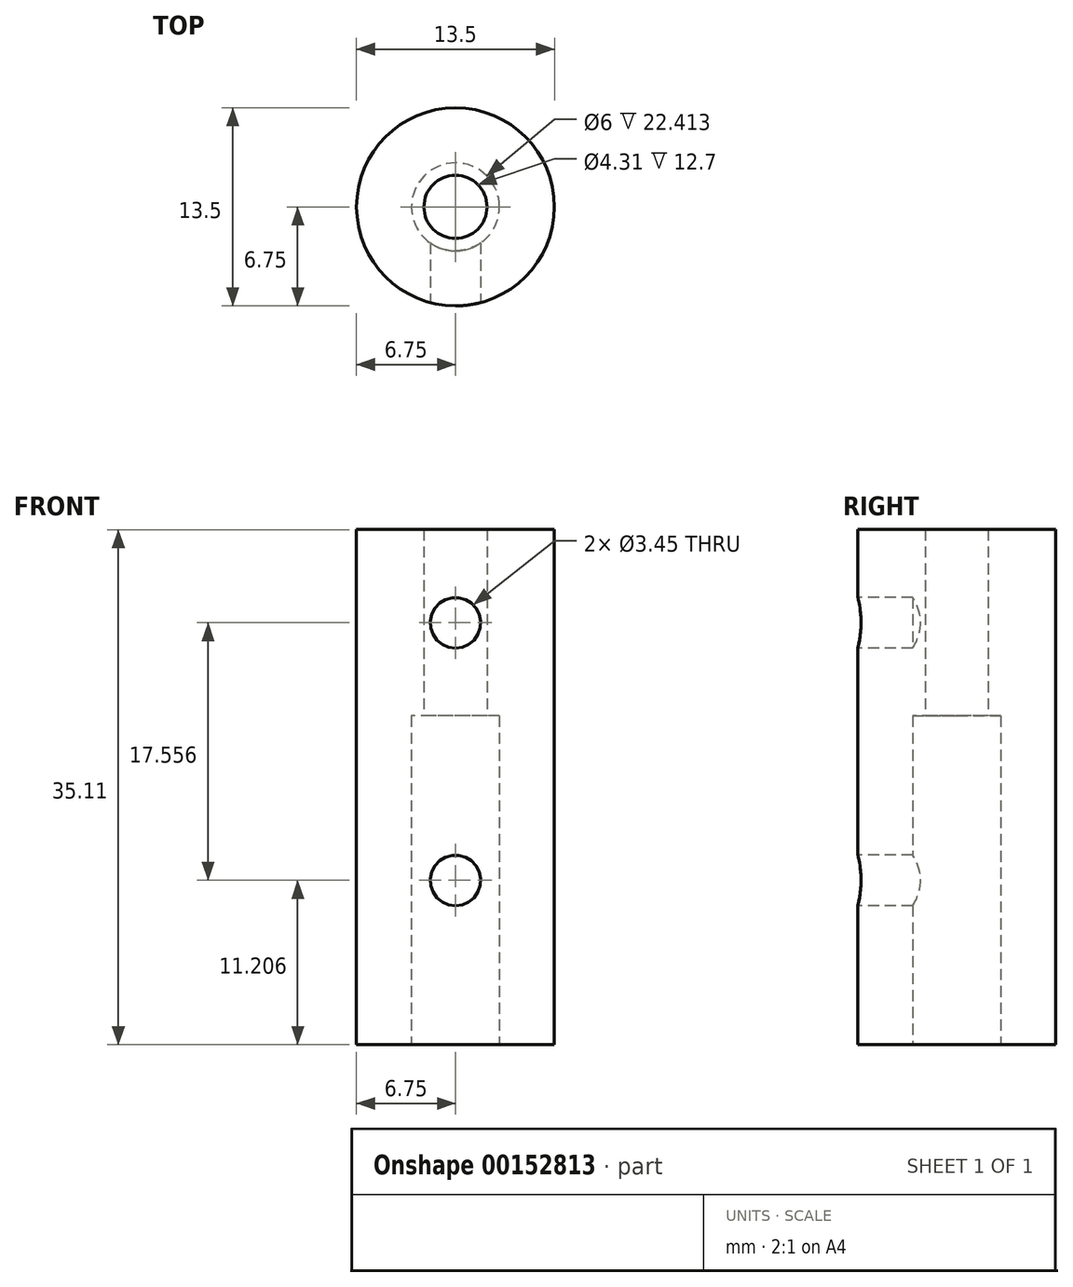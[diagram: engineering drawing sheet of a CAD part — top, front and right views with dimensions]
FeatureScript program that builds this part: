
annotation { "Feature Type Name" : "Feature", "Feature Type Description" : "" }
export const myFeature = defineFeature(function(context is Context, id is Id, definition is map)
    precondition{}
    {
        {
            var Q0;
            Q0=qCreatedBy(makeId("Top.planeOp"),FACE);
            var sketch = newSketch(context, id + "F0", { "sketchPlane" : qUnion([Q0])});
            skLineSegment(sketch, "E0.bottom", {"start": v(12.7, -12.7) * mm, "end": v(-12.7, -12.7) * mm});
            skLineSegment(sketch, "E0.top", {"start": v(12.7, 12.7) * mm, "end": v(-12.7, 12.7) * mm});
            skLineSegment(sketch, "E0.left", {"start": v(12.7, -12.7) * mm, "end": v(12.7, 12.7) * mm});
            skLineSegment(sketch, "E0.right", {"start": v(-12.7, -12.7) * mm, "end": v(-12.7, 12.7) * mm});
            skPoint(sketch, "E0.middle", {"position": v(0, 0) * mm});
            skCircle(sketch, "E1", {"center": v(0, 0) * mm, "radius": 12.7 * mm, "construction": true});
            skCircle(sketch, "E2", {"center": v(0, 0) * mm, "radius": 3 * mm});
            skCircle(sketch, "E3", {"center": v(0, 0) * mm, "radius": 3.18 * mm, "construction": true});
            skSolve(sketch);
        }
        {
            var Q0;
            Q0 = qSketchRegion(id + "F0", true);
            extrude(context, id + "F1", {"entities" : qUnion([Q0]), "depth" : 22.41 * mm});
        }
        {
            var Q0;
            Q0=makeQuery(id+"F1.opExtrude","CAP_FACE",FACE,{"disambiguationData":[OSD([sQuery(id+"F0.wireOp",EDGE,"E0.bottom"),sQuery(id+"F0.wireOp",EDGE,"E0.top"),sQuery(id+"F0.wireOp",EDGE,"E0.left"),sQuery(id+"F0.wireOp",EDGE,"E0.right"),sQuery(id+"F0.wireOp",EDGE,"E2")])],"isStart":false});
            var sketch = newSketch(context, id + "F2", { "sketchPlane" : qUnion([Q0])});
            skCircle(sketch, "E4", {"center": v(0, 0) * mm, "radius": 2.15 * mm});
            skSolve(sketch);
        }
        {
            var Q0;
            Q0=makeQuery(id+"F2.imprint","IMPRINT",FACE,{"disambiguationData":[TD([[makeQuery(id+"F2.imprint","IMPRINT",EDGE,{"derivedFrom":sQuery(id+"F2.wireOp",EDGE,"E4")}),-1.0]])]});
            var Q1;
            Q1=makeQuery(id+"F2.imprint","IMPRINT",FACE,{"disambiguationData":[TD([[makeQuery(id+"F2.imprint","IMPRINT",EDGE,{"derivedFrom":makeQuery(id+"F1.opExtrude","CAP_EDGE",EDGE,{"disambiguationData":[OSD([sQuery(id+"F0.wireOp",EDGE,"E0.bottom")])],"isStart":false})}),-1.0]])]});
            extrude(context, id + "F3", {"entities" : qUnion([Q0, Q1]), "operationType" : NewBodyOperationType.ADD, "depth" : 12.7 * mm});
        }
        {
            var Q0;
            {var subQ0=sQuery(id+"F0.wireOp",EDGE,"E0.bottom");Q0=makeQuery(id+"F3.boolean.opBoolean","MERGE",FACE,{"derivedFrom":[makeQuery(id+"F1.opExtrude","SWEPT_FACE",FACE,{"disambiguationData":[OSD([subQ0])]}),makeQuery(id+"F3.opExtrude","SWEPT_FACE",FACE,{"disambiguationData":[OSD([subQ0])]})]});}
            var sketch = newSketch(context, id + "F4", { "sketchPlane" : qUnion([Q0])});
            skLineSegment(sketch, "E5", {"start": v(0, 35.11) * mm, "end": v(0, 22.41) * mm, "construction": true});
            skLineSegment(sketch, "E6", {"start": v(0, 22.41) * mm, "end": v(0, 0) * mm, "construction": true});
            skCircle(sketch, "E7", {"center": v(0, 28.76) * mm, "radius": 1.73 * mm});
            skCircle(sketch, "E8", {"center": v(0, 11.2) * mm, "radius": 1.73 * mm});
            skSolve(sketch);
        }
        {
            var Q0;
            Q0 = qSketchRegion(id + "F4", true);
            var Q1;
            Q1=makeQuery(id+"F1.opExtrude","SWEPT_FACE",FACE,{"disambiguationData":[OSD([sQuery(id+"F0.wireOp",EDGE,"E2")])]});
            extrude(context, id + "F5", {"entities" : qUnion([Q0]), "operationType" : NewBodyOperationType.REMOVE, "endBound" : BoundingType.UP_TO_SURFACE, "oppositeDirection" : true, "endBoundEntityFace" : qUnion([Q1]), "depth" : 25.4 * mm});
        }
        {
            var Q0;
            Q0=makeQuery(id+"F3.opExtrude","CAP_FACE",FACE,{"disambiguationData":[OSD([sQuery(id+"F0.wireOp",EDGE,"E0.bottom"),sQuery(id+"F0.wireOp",EDGE,"E0.top"),sQuery(id+"F0.wireOp",EDGE,"E0.left"),sQuery(id+"F0.wireOp",EDGE,"E0.right"),sQuery(id+"F2.wireOp",EDGE,"E4")])],"isStart":false});
            var sketch = newSketch(context, id + "F6", { "sketchPlane" : qUnion([Q0])});
            skLineSegment(sketch, "E9.bottom", {"start": v(-12.7, 12.7) * mm, "end": v(12.7, 12.7) * mm});
            skLineSegment(sketch, "E9.top", {"start": v(-12.7, -12.7) * mm, "end": v(12.7, -12.7) * mm});
            skLineSegment(sketch, "E9.left", {"start": v(-12.7, 12.7) * mm, "end": v(-12.7, -12.7) * mm});
            skLineSegment(sketch, "E9.right", {"start": v(12.7, 12.7) * mm, "end": v(12.7, -12.7) * mm});
            skCircle(sketch, "E10", {"center": v(0, 0) * mm, "radius": 6.75 * mm});
            skSolve(sketch);
        }
        {
            var Q0;
            Q0 = qSketchRegion(id + "F6", true);
            var Q1;
            Q1=makeQuery(id+"F1.opExtrude","CAP_FACE",FACE,{"disambiguationData":[OSD([sQuery(id+"F0.wireOp",EDGE,"E0.bottom"),sQuery(id+"F0.wireOp",EDGE,"E0.top"),sQuery(id+"F0.wireOp",EDGE,"E0.left"),sQuery(id+"F0.wireOp",EDGE,"E0.right"),sQuery(id+"F0.wireOp",EDGE,"E2")])],"isStart":true});
            extrude(context, id + "F7", {"entities" : qUnion([Q0]), "operationType" : NewBodyOperationType.REMOVE, "endBound" : BoundingType.UP_TO_SURFACE, "oppositeDirection" : true, "endBoundEntityFace" : qUnion([Q1]), "depth" : 25.4 * mm});
        }
    });
